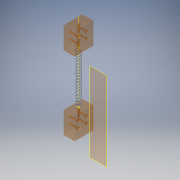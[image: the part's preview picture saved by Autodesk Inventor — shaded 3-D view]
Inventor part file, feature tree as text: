
AUTODESK INVENTOR PART (.ipt)
format: ipt  version: 2016 (Build 200138000, 138)  size: 370,176 bytes
history: native  units: in
note: dims shown in document units (in); Inventor stores cm internally (conversion verified against a paired STEP export)
features: other x5, surface_op x2, plane x1, helix x1, sketch x1
ambient origin geometry x8: Origin, YZ Plane, XZ Plane, XY Plane, X Axis, Y Axis, Z Axis, Center Point
bodies: Solid1 (feature_tree)
feature tree (10):
  other  "Work Axis1"
  other  "Work Point1"
  other  "Work Point2"
  plane  "Work Plane1"
  helix  "Coil1"  [1 undecoded]
  sketch  "Sketch1"  dims[d1=0.195in d2=4.2456in d3=1.0in d4=4.1976in d5=7.4803in d6=0.0in d7=90.0deg d8=90.0deg d9=0.0in d10=0.0in]
  surface_op  "Surface1"
  surface_op  "Surface2"
  other  "Srf1"
  other  "Srf2"
note: 1 required parameter value undecoded (feature->parameter linkage not recoverable at this tier; creation-order binding heuristic only, values carry confidence <= 0.55)
